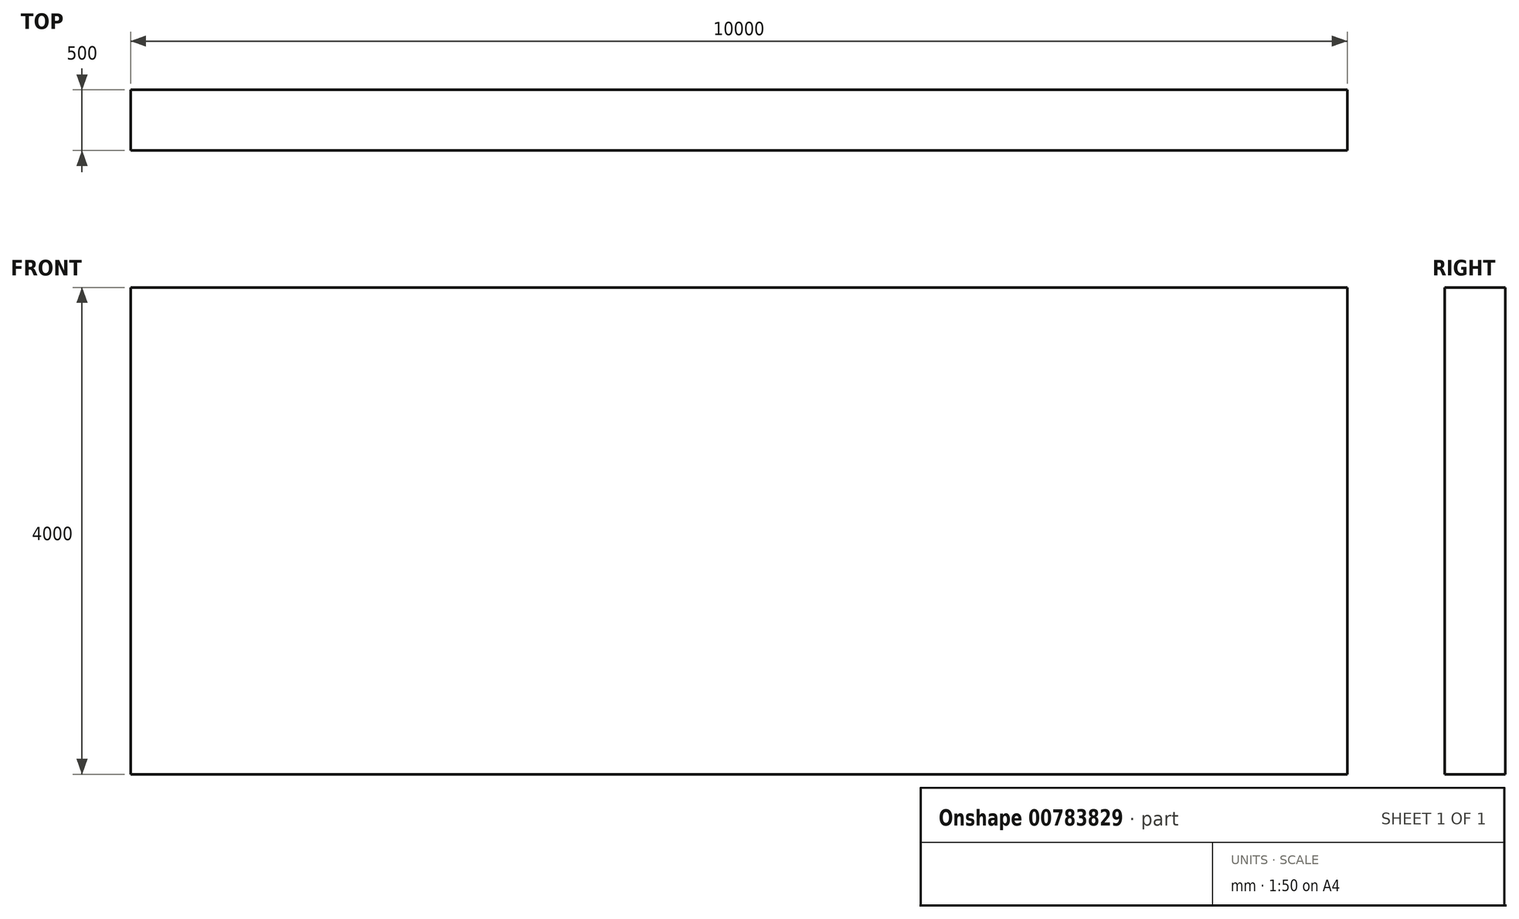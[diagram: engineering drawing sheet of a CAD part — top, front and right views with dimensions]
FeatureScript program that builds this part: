
annotation { "Feature Type Name" : "Feature", "Feature Type Description" : "" }
export const myFeature = defineFeature(function(context is Context, id is Id, definition is map)
    precondition{}
    {
        {
            var Q0;
            Q0=qCreatedBy(makeId("Top.planeOp"),FACE);
            var sketch = newSketch(context, id + "F0", { "sketchPlane" : qUnion([Q0])});
            skLineSegment(sketch, "E0.bottom", {"start": v(-5000, -250) * mm, "end": v(5000, -250) * mm});
            skLineSegment(sketch, "E0.top", {"start": v(-5000, 250) * mm, "end": v(5000, 250) * mm});
            skLineSegment(sketch, "E0.left", {"start": v(-5000, -250) * mm, "end": v(-5000, 250) * mm});
            skLineSegment(sketch, "E0.right", {"start": v(5000, -250) * mm, "end": v(5000, 250) * mm});
            skPoint(sketch, "E0.middle", {"position": v(0, 0) * mm});
            skSolve(sketch);
        }
        {
            var Q0;
            Q0=makeQuery(id+"F0.imprint","IMPRINT",FACE,{"disambiguationData":[TD([[makeQuery(id+"F0.imprint","IMPRINT",EDGE,{"derivedFrom":sQuery(id+"F0.wireOp",EDGE,"E0.bottom")}),1.0]])]});
            extrude(context, id + "F1", {"entities" : qUnion([Q0]), "depth" : 4000 * mm, "offsetDistance" : 25 * mm});
        }
    });
